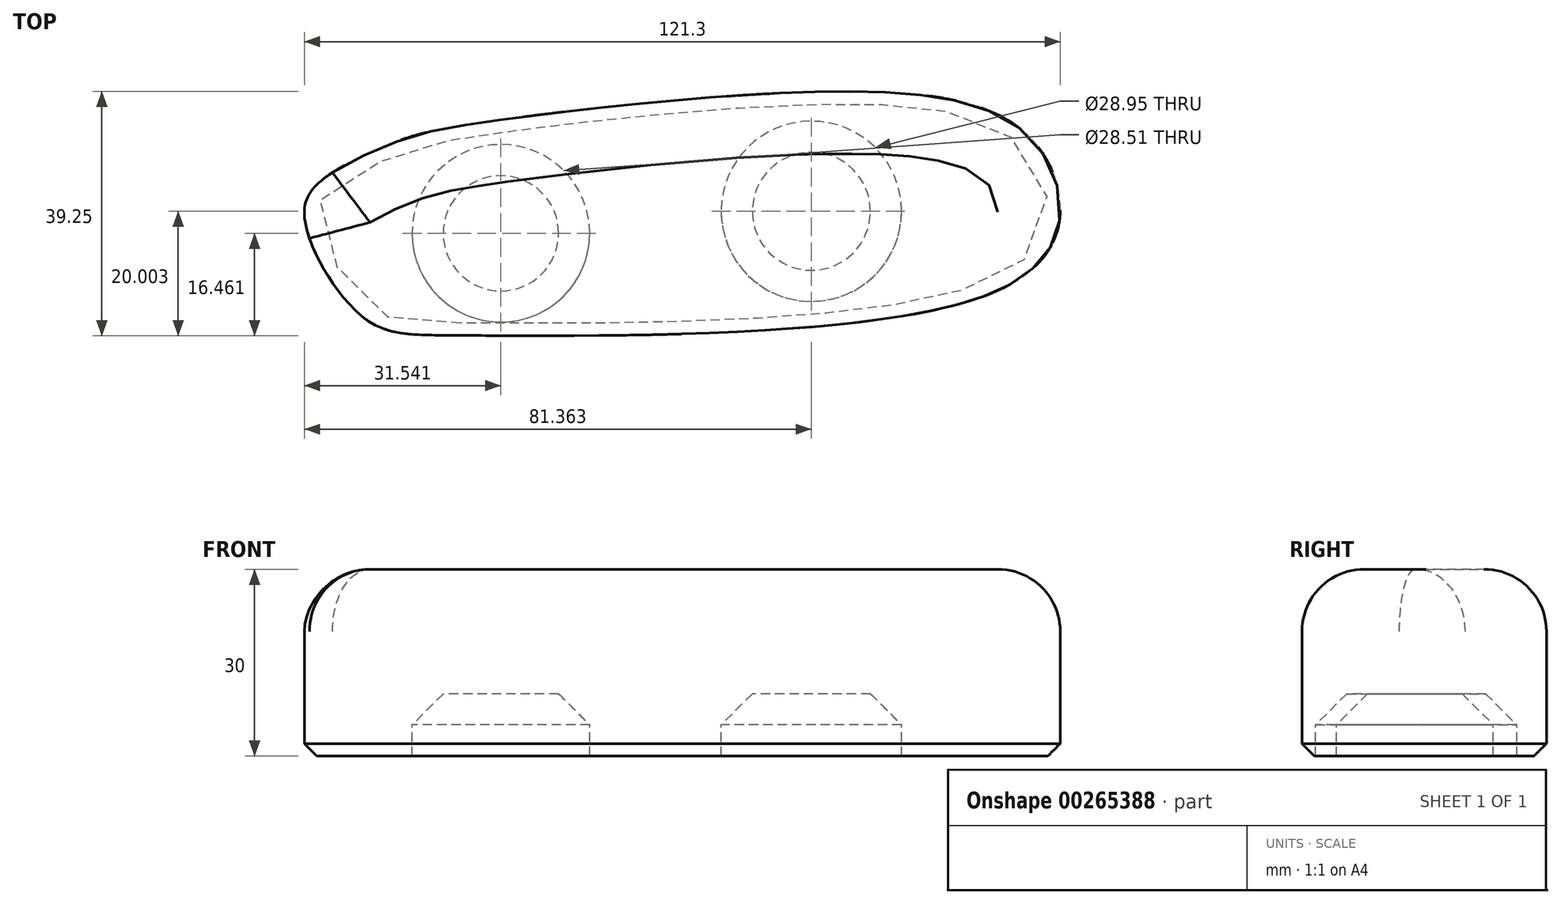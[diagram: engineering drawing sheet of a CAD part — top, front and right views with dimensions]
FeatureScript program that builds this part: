
annotation { "Feature Type Name" : "Feature", "Feature Type Description" : "" }
export const myFeature = defineFeature(function(context is Context, id is Id, definition is map)
    precondition{}
    {
        {
            var Q0;
            Q0=qCreatedBy(makeId("Top.planeOp"),FACE);
            var sketch = newSketch(context, id + "F0", { "sketchPlane" : qUnion([Q0])});
            skFitSpline(sketch, "E0", {"points": [v(-38.6, -12.6) * mm, v(-54.9, -9.12) * mm, v(-63.62, 6.6) * mm, v(-59.94, 13) * mm, v(-48.5, 18.66) * mm, v(-35.3, 21.57) * mm, v(24.63, 26.57) * mm, v(51.98, 19.98) * mm, v(57.64, 6.72) * mm, v(44.61, -6.6) * mm, v(-38.6, -12.6) * mm]});
            skSolve(sketch);
        }
        {
            var Q0;
            Q0=makeQuery(id+"F0.imprint","IMPRINT",FACE,{"disambiguationData":[TD([[makeQuery(id+"F0.imprint","IMPRINT",EDGE,{"derivedFrom":sQuery(id+"F0.wireOp",EDGE,"E0")}),-1.0]])]});
            extrude(context, id + "F1", {"entities" : qUnion([Q0]), "depth" : 20 * mm});
        }
        {
            var Q0;
            Q0=makeQuery(id+"F1.opExtrude","CAP_FACE",FACE,{"disambiguationData":[OSD([sQuery(id+"F0.wireOp",EDGE,"E0")])],"isStart":false});
            fillet(context, id + "F2", {"entities" : qUnion([Q0]), "radius" : 10 * mm, "tangentPropagation" : true, "allowEdgeOverflow" : false});
        }
        {
            var Q0;
            Q0=makeQuery(id+"F1.opExtrude","CAP_FACE",FACE,{"disambiguationData":[OSD([sQuery(id+"F0.wireOp",EDGE,"E0")])],"isStart":true});
            var sketch = newSketch(context, id + "F3", { "sketchPlane" : qUnion([Q0])});
            skCircle(sketch, "E1", {"center": v(-32.09, -3.8) * mm, "radius": 14.26 * mm});
            skCircle(sketch, "E2", {"center": v(17.73, -7.33) * mm, "radius": 14.48 * mm});
            skSolve(sketch);
        }
        {
            var Q0;
            Q0=makeQuery(id+"F3.imprint","IMPRINT",FACE,{"disambiguationData":[TD([[makeQuery(id+"F3.imprint","IMPRINT",EDGE,{"derivedFrom":sQuery(id+"F3.wireOp",EDGE,"E1")}),-1.0]])]});
            extrude(context, id + "F4", {"entities" : qUnion([Q0]), "operationType" : NewBodyOperationType.ADD, "depth" : 10 * mm});
        }
        {
            var Q0;
            Q0=makeQuery(id+"F4.boolean.opBoolean","SPLIT",FACE,{"disambiguationData":[TD([makeQuery(id+"F4.opExtrude","SWEPT_FACE",FACE,{"disambiguationData":[OSD([sQuery(id+"F3.wireOp",EDGE,"E2")])]})])],"derivedFrom":makeQuery(id+"F1.opExtrude","CAP_FACE",FACE,{"disambiguationData":[OSD([sQuery(id+"F0.wireOp",EDGE,"E0")])],"isStart":true})});
            var Q1;
            Q1=makeQuery(id+"F4.boolean.opBoolean","SPLIT",FACE,{"disambiguationData":[TD([makeQuery(id+"F4.opExtrude","SWEPT_FACE",FACE,{"disambiguationData":[OSD([sQuery(id+"F3.wireOp",EDGE,"E1")])]})])],"derivedFrom":makeQuery(id+"F1.opExtrude","CAP_FACE",FACE,{"disambiguationData":[OSD([sQuery(id+"F0.wireOp",EDGE,"E0")])],"isStart":true})});
            chamfer(context, id + "F5", {"entities" : qUnion([Q0, Q1]), "width" : 5 * mm, "tangentPropagation" : true});
        }
        {
            var Q0;
            Q0=makeQuery(id+"F4.opExtrude","CAP_EDGE",EDGE,{"disambiguationData":[OSD([sQuery(id+"F0.wireOp",EDGE,"E0")])],"isStart":false});
            chamfer(context, id + "F6", {"entities" : qUnion([Q0]), "width" : 2 * mm, "tangentPropagation" : true});
        }
    });
